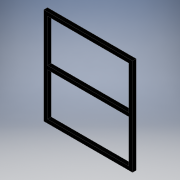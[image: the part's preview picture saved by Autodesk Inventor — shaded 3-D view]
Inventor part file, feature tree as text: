
AUTODESK INVENTOR PART (.ipt)
format: ipt  version: 2016 (Build 200138000, 138)  size: 105,472 bytes
history: native  units: in
note: dims shown in document units (in); Inventor stores cm internally (conversion verified against a paired STEP export)
features: extrude x1, sketch x1
ambient origin geometry x8: Origin, YZ Plane, XZ Plane, XY Plane, X Axis, Y Axis, Z Axis, Center Point
bodies: Solid1 (feature_tree)
feature tree (2):
  extrude  "Extrusion1"  Depth=44.0in
  sketch  "Sketch1"  dims[d0=48.0in d2=44.0in d3=48.25in d4=2.0in d5=2.0in d6=0.0in]
